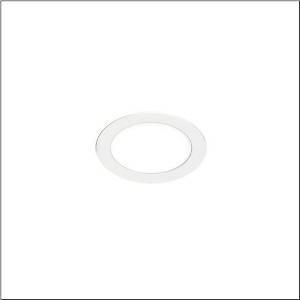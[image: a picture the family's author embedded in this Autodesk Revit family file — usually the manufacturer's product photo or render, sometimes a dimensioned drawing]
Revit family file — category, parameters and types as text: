
# Revit family: lunis_41_flat_51dr10ddgbb
name_source: partatom
category: Lighting Fixtures
units: mm (PartAtom-declared; Revit-internal decimal feet)

## family parameters
Cut with Voids When Loaded = No
Host = Face
Light Source = No
Part Type = Normal
Room Calculation Point = No
Round Connector Dimension = Use Diameter
Shared = No

## types (1)
- --- (1 x LED, 1750 lm, 14 W, 4000K)
    Apparent Load = 14 VA
    CIE Flux Codes = 49 80 96 100 100
    Color Rendering = 80
    Color Temperature = 4000K
    Default Elevation = 1800 mm
    Description = Lunis 41,  Flat, downlight, light emission: direct distribution, LED rated luminous flux: 1.575lm, light colour: 830/840, control gear: ECG, mains connection: 230V, AC, 50/60Hz, housing, round, of aluminium, coated, traffic white (RAL 9016), diameter: 170mm, protection rating (complete): IP20, protection rating (on room side): IP44, insulation class (complete): insulation class II (safety insulation), certification: CE, permissible ambient temperature for indoor applications: -20..+40°C, packaging unit: 1 piece
    Height = 0 mm  [stored 0 ft]
    Lamp = 1 x LED
    Lamp Light Flux = 1750 lm
    Lamp Power = 14 W
    Lamp count = 1
    Length = 170 mm  [stored 0.557743 ft]
    Luminous efficacy = 125 lm/W
    Manufacturer = Siteco
    ModVariant = No
    Model = 51DR10DDGBB
    Mounting Place = Ceiling
    Mounting Type = Recessed
    Number of Poles = 1
    OnlyDefault = Yes
    Power Factor = 1
    Product Name = Lunis 41 Flat
    Product group = downlight
    ProductGroupID = 401
    Protection Class = Protection class II
    Protection Degree = IP 20
    RLX_Detail_Level = 1
    RLX_Emergency_Light_Flux = 0 lm
    RLX_Emergency_Type = 0
    RLX_Emergency_Type_DB = No
    RlxData = <blob elided: 10885 chars, md5=0449e9ed>
    Socket = socket
    Standby Power = 0 W
    System Light Flux = 1750 lm
    System Power = 14 W
    Type Comments = factory setting: colour temperature 4000K, luminous flux: 100 % | (ON | ON) | 350 mA
    Type Image = l_1340921.jpg
    URL = http://relux.com
    VarID = @adj_018919
    Voltage = 0 V
    Weight = 0.00 kg
    Width = 0 mm  [stored 0 ft]

note: [stored X ft] marks values corroborated as IEEE doubles in the binary element streams (Revit-internal decimal feet)

## geometry (parser evidence)
native form markers: Sweep x7
no freeform markers — native parametric forms only
